# Revit family: FantiniCosmi_BIM_7P1-XR306-00A
name_source: partatom
category: Generic Models
units: mm (PartAtom-declared; Revit-internal decimal feet)

## family parameters
Always vertical = Yes
Can host rebar = No
Cut with Voids When Loaded = No
Part Type = Normal
Room Calculation Point = No
Round Connector Dimension = Use Diameter
Shared = No
Work Plane-Based = No

## types (1)
- Standard
    Approvals = ISPESL - ENEC 03 - CE 0497
    Catalog web link = https://www.fantinicosmi.it
    Connection = R 1/2
    Default Elevation = 0 mm  [stored 0 ft]
    Degree of protection = IP43
    Description = Immersion limit thermostat
    Designer = Carniti
    Device earthing = screw clamp
    Differential = 6±2°C
    Pack QTY = 10
    Part Number = 7P1-XR306-00A
    Pollution level of the control device = 2
    Rated impulsive voltage = 4 kV
    Regualation Range = 30 ÷ 70 °C
    Regualation Type = external
    Sheath = 100 mm
    Temperature limit of thermostat head = T 85
    Thermal gradient = 1°C/min
    To be used heat resistant cables = min. T 140
    Tollerance = temp.min. ±6°C temp. max. ±4°C
    Type of action = 1B

note: [stored X ft] marks values corroborated as IEEE doubles in the binary element streams (Revit-internal decimal feet)

## geometry (parser evidence)
native form markers: Sweep x2
no freeform markers — native parametric forms only
